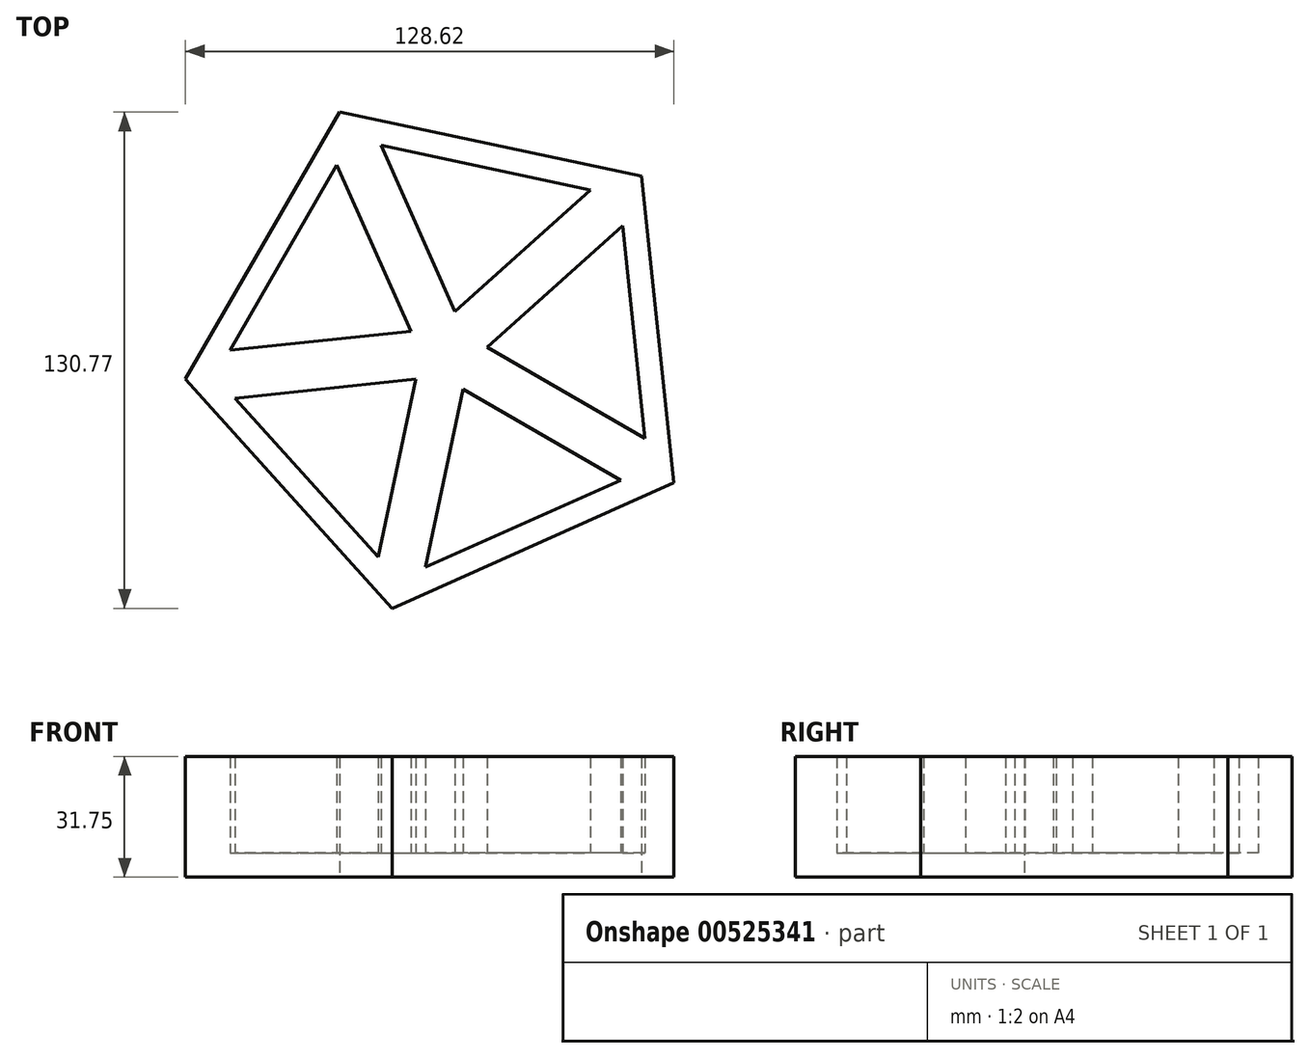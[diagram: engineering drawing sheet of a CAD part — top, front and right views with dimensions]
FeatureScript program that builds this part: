
annotation { "Feature Type Name" : "Feature", "Feature Type Description" : "" }
export const myFeature = defineFeature(function(context is Context, id is Id, definition is map)
    precondition{}
    {
        {
            var Q0;
            Q0=qCreatedBy(makeId("Top.planeOp"),FACE);
            var sketch = newSketch(context, id + "F0", { "sketchPlane" : qUnion([Q0])});
            skCircle(sketch, "E0.cCircle", {"center": v(0, 0) * mm, "radius": 55.93 * mm, "construction": true});
            skLineSegment(sketch, "E0.0", {"start": v(-68.75, -7.24) * mm, "end": v(-28.13, 63.15) * mm});
            skLineSegment(sketch, "E0.1", {"start": v(-28.13, 63.15) * mm, "end": v(51.37, 46.27) * mm});
            skLineSegment(sketch, "E0.2", {"start": v(51.37, 46.27) * mm, "end": v(59.87, -34.55) * mm});
            skLineSegment(sketch, "E0.3", {"start": v(59.87, -34.55) * mm, "end": v(-14.36, -67.62) * mm});
            skLineSegment(sketch, "E0.4", {"start": v(-14.36, -67.62) * mm, "end": v(-68.75, -7.24) * mm});
            skPoint(sketch, "E0.0.midPoint", {"position": v(-48.44, 27.96) * mm});
            skLineSegment(sketch, "E1", {"start": v(-28.13, 63.15) * mm, "end": v(0, 0) * mm});
            skLineSegment(sketch, "E2", {"start": v(51.37, 46.27) * mm, "end": v(0, 0) * mm});
            skLineSegment(sketch, "E3", {"start": v(-68.75, -7.24) * mm, "end": v(0, 0) * mm});
            skLineSegment(sketch, "E4", {"start": v(59.87, -34.55) * mm, "end": v(0, 0) * mm});
            skLineSegment(sketch, "E5", {"start": v(-14.36, -67.62) * mm, "end": v(0, 0) * mm});
            skLineSegment(sketch, "E6.0", {"start": v(-28.86, 49.18) * mm, "end": v(-9.36, 5.4) * mm});
            skLineSegment(sketch, "E7.trimOffspring", {"start": v(-57.02, 0.38) * mm, "end": v(-9.36, 5.4) * mm});
            skLineSegment(sketch, "E8.trimOffspring", {"start": v(-57.02, 0.38) * mm, "end": v(-28.86, 49.18) * mm});
            skLineSegment(sketch, "E9.0", {"start": v(37.86, 42.64) * mm, "end": v(2.24, 10.57) * mm});
            skLineSegment(sketch, "E10.0", {"start": v(-17.26, 54.35) * mm, "end": v(37.86, 42.64) * mm});
            skLineSegment(sketch, "E11.0", {"start": v(52.25, -22.83) * mm, "end": v(10.74, 1.13) * mm});
            skLineSegment(sketch, "E12.0", {"start": v(45.9, -33.83) * mm, "end": v(4.4, -9.87) * mm});
            skLineSegment(sketch, "E13.0", {"start": v(-5.56, -56.75) * mm, "end": v(4.4, -9.87) * mm});
            skLineSegment(sketch, "E14.0", {"start": v(45.9, -33.83) * mm, "end": v(-5.56, -56.75) * mm});
            skLineSegment(sketch, "E15.0", {"start": v(-55.7, -12.25) * mm, "end": v(-8.03, -7.23) * mm});
            skLineSegment(sketch, "E16.trimOffspring", {"start": v(-17.26, 54.35) * mm, "end": v(2.24, 10.57) * mm});
            skLineSegment(sketch, "E17.trimOffspring", {"start": v(46.36, 33.2) * mm, "end": v(10.74, 1.13) * mm});
            skLineSegment(sketch, "E18.trimOffspring", {"start": v(46.36, 33.2) * mm, "end": v(52.25, -22.83) * mm});
            skLineSegment(sketch, "E19.trimOffspring", {"start": v(-17.98, -54.11) * mm, "end": v(-55.7, -12.25) * mm});
            skLineSegment(sketch, "E20.trimOffspring", {"start": v(-17.98, -54.11) * mm, "end": v(-8.03, -7.23) * mm});
            skSolve(sketch);
        }
        {
            var Q0;
            Q0=makeQuery(id+"F0.imprint","IMPRINT",FACE,{"disambiguationData":[TD([[makeQuery(id+"F0.imprint","IMPRINT",EDGE,{"derivedFrom":sQuery(id+"F0.wireOp",EDGE,"E0.3")}),-1.0]])]});
            var Q1;
            Q1=makeQuery(id+"F0.imprint","IMPRINT",FACE,{"disambiguationData":[TD([[makeQuery(id+"F0.imprint","IMPRINT",EDGE,{"derivedFrom":sQuery(id+"F0.wireOp",EDGE,"E0.4")}),-1.0]])]});
            var Q2;
            Q2=makeQuery(id+"F0.imprint","IMPRINT",FACE,{"disambiguationData":[TD([[makeQuery(id+"F0.imprint","IMPRINT",EDGE,{"derivedFrom":sQuery(id+"F0.wireOp",EDGE,"E0.1")}),-1.0]])]});
            var Q3;
            Q3=makeQuery(id+"F0.imprint","IMPRINT",FACE,{"disambiguationData":[TD([[makeQuery(id+"F0.imprint","IMPRINT",EDGE,{"derivedFrom":sQuery(id+"F0.wireOp",EDGE,"E0.2")}),-1.0]])]});
            extrude(context, id + "F1", {"entities" : qUnion([Q0, Q1, Q2, Q3]), "depth" : 25.4 * mm, "offsetDistance" : 25.4 * mm});
        }
        {
            var Q0;
            Q0 = qSketchRegion(id + "F0", true);
            extrude(context, id + "F2", {"entities" : qUnion([Q0]), "operationType" : NewBodyOperationType.ADD, "depth" : 25.4 * mm, "offsetDistance" : 25.4 * mm});
        }
        {
            var Q0;
            {var subQ0=sQuery(id+"F0.wireOp",EDGE,"E20.trimOffspring");var subQ1=sQuery(id+"F0.wireOp",EDGE,"E19.trimOffspring");var subQ2=sQuery(id+"F0.wireOp",EDGE,"E11.0");var subQ3=sQuery(id+"F0.wireOp",EDGE,"E18.trimOffspring");var subQ4=sQuery(id+"F0.wireOp",EDGE,"E17.trimOffspring");var subQ5=sQuery(id+"F0.wireOp",EDGE,"E16.trimOffspring");var subQ6=sQuery(id+"F0.wireOp",EDGE,"E15.0");var subQ7=sQuery(id+"F0.wireOp",EDGE,"E14.0");var subQ8=sQuery(id+"F0.wireOp",EDGE,"E13.0");var subQ9=sQuery(id+"F0.wireOp",EDGE,"E12.0");var subQ10=sQuery(id+"F0.wireOp",EDGE,"E10.0");var subQ11=sQuery(id+"F0.wireOp",EDGE,"E9.0");var subQ12=sQuery(id+"F0.wireOp",EDGE,"E0.4");var subQ13=sQuery(id+"F0.wireOp",EDGE,"E0.3");var subQ14=sQuery(id+"F0.wireOp",EDGE,"E0.2");var subQ15=sQuery(id+"F0.wireOp",EDGE,"E0.1");Q0=makeQuery(id+"F2.boolean.opBoolean","MERGE",FACE,{"derivedFrom":[makeQuery(id+"F1.opExtrude","CAP_FACE",FACE,{"disambiguationData":[OSD([subQ15,subQ14,subQ13,subQ12,sQuery(id+"F0.wireOp",EDGE,"E1"),sQuery(id+"F0.wireOp",EDGE,"E3"),subQ11,subQ10,subQ9,subQ8,subQ7,subQ6,subQ5,subQ4,subQ3,subQ2,subQ1,subQ0])],"isStart":true}),makeQuery(id+"F2.opExtrude","CAP_FACE",FACE,{"disambiguationData":[OSD([sQuery(id+"F0.wireOp",EDGE,"E0.0"),subQ15,subQ14,subQ13,subQ12,sQuery(id+"F0.wireOp",EDGE,"E6.0"),sQuery(id+"F0.wireOp",EDGE,"E7.trimOffspring"),sQuery(id+"F0.wireOp",EDGE,"E8.trimOffspring"),subQ11,subQ10,subQ9,subQ8,subQ7,subQ6,subQ5,subQ4,subQ3,subQ2,subQ1,subQ0])],"isStart":true})]});}
            var sketch = newSketch(context, id + "F3", { "sketchPlane" : qUnion([Q0])});
            skLineSegment(sketch, "E21", {"start": v(-28.13, -63.15) * mm, "end": v(51.37, -46.27) * mm});
            skLineSegment(sketch, "E22", {"start": v(51.37, -46.27) * mm, "end": v(59.87, 34.55) * mm});
            skLineSegment(sketch, "E23", {"start": v(59.87, 34.55) * mm, "end": v(-14.36, 67.62) * mm});
            skLineSegment(sketch, "E24", {"start": v(-14.36, 67.62) * mm, "end": v(-68.75, 7.24) * mm});
            skLineSegment(sketch, "E25", {"start": v(-68.75, 7.24) * mm, "end": v(-28.13, -63.15) * mm});
            skSolve(sketch);
        }
        {
            var Q0;
            Q0 = qSketchRegion(id + "F3", true);
            extrude(context, id + "F4", {"entities" : qUnion([Q0]), "operationType" : NewBodyOperationType.ADD, "depth" : 6.35 * mm, "offsetDistance" : 25.4 * mm});
        }
    });
